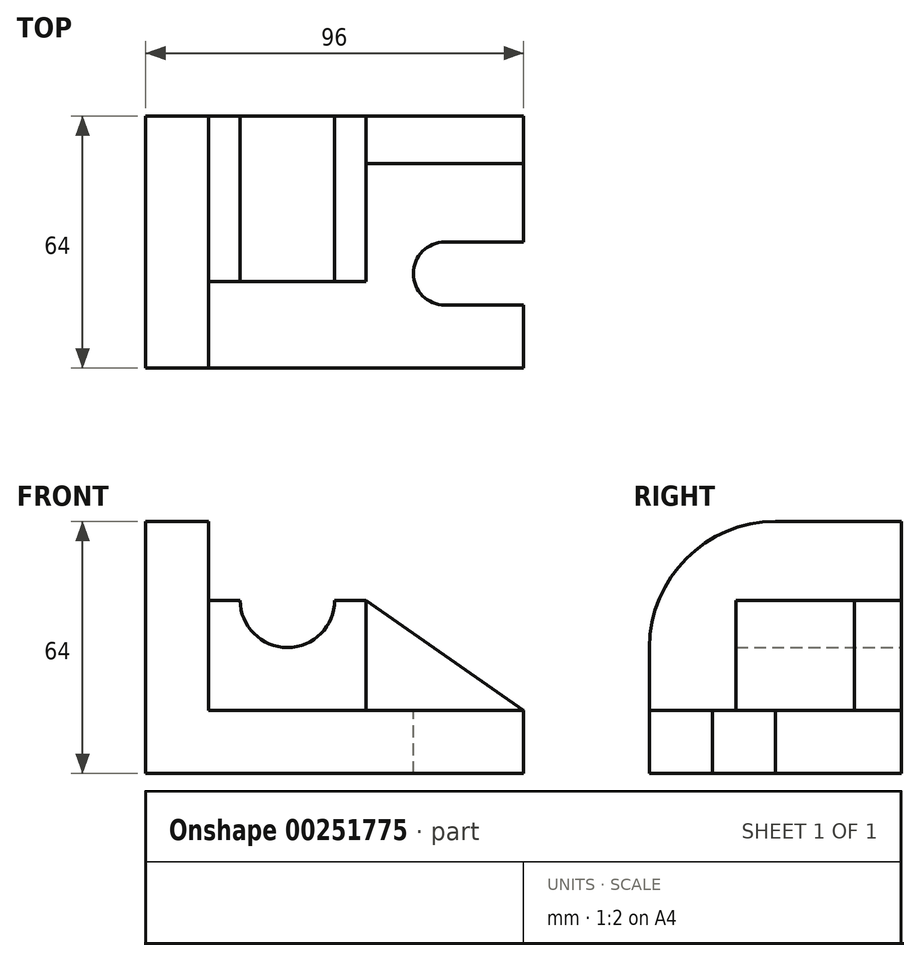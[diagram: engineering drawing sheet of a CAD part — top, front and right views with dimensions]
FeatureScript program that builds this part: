
annotation { "Feature Type Name" : "Feature", "Feature Type Description" : "" }
export const myFeature = defineFeature(function(context is Context, id is Id, definition is map)
    precondition{}
    {
        {
            var Q0;
            Q0=qCreatedBy(makeId("Front.planeOp"),FACE);
            var sketch = newSketch(context, id + "F0", { "sketchPlane" : qUnion([Q0])});
            skLineSegment(sketch, "E0.bottom", {"start": v(48, -8) * mm, "end": v(-48, -8) * mm});
            skLineSegment(sketch, "E0.top", {"start": v(48, 8) * mm, "end": v(-48, 8) * mm});
            skLineSegment(sketch, "E0.left", {"start": v(48, -8) * mm, "end": v(48, 8) * mm});
            skLineSegment(sketch, "E0.right", {"start": v(-48, -8) * mm, "end": v(-48, 8) * mm});
            skPoint(sketch, "E0.middle", {"position": v(0, 0) * mm});
            skLineSegment(sketch, "E1.bottom", {"start": v(-48, 8) * mm, "end": v(-32, 8) * mm});
            skLineSegment(sketch, "E1.top", {"start": v(-48, 56) * mm, "end": v(-32, 56) * mm});
            skLineSegment(sketch, "E1.left", {"start": v(-48, 8) * mm, "end": v(-48, 56) * mm});
            skLineSegment(sketch, "E1.right", {"start": v(-32, 8) * mm, "end": v(-32, 56) * mm});
            skSolve(sketch);
        }
        {
            var Q0;
            Q0 = qSketchRegion(id + "F0", true);
            extrude(context, id + "F1", {"entities" : qUnion([Q0]), "endBound" : BoundingType.SYMMETRIC, "oppositeDirection" : true, "depth" : 64 * mm});
        }
        {
            var Q0;
            Q0=makeQuery(id+"F1.opExtrude","CAP_EDGE",EDGE,{"disambiguationData":[OSD([sQuery(id+"F0.wireOp",EDGE,"E1.top")])],"isStart":true});
            fillet(context, id + "F2", {"entities" : qUnion([Q0]), "radius" : 32 * mm, "tangentPropagation" : true, "allowEdgeOverflow" : false});
        }
        {
            var Q0;
            Q0=makeQuery(id+"F1.opExtrude","CAP_FACE",FACE,{"disambiguationData":[OSD([sQuery(id+"F0.wireOp",EDGE,"E0.bottom"),sQuery(id+"F0.wireOp",EDGE,"E0.top"),sQuery(id+"F0.wireOp",EDGE,"E0.left"),sQuery(id+"F0.wireOp",EDGE,"E0.right"),sQuery(id+"F0.wireOp",EDGE,"E1.top"),sQuery(id+"F0.wireOp",EDGE,"E1.left"),sQuery(id+"F0.wireOp",EDGE,"E1.right")])],"isStart":false});
            var sketch = newSketch(context, id + "F3", { "sketchPlane" : qUnion([Q0])});
            skLineSegment(sketch, "E2", {"start": v(32, 36) * mm, "end": v(-8, 36) * mm});
            skLineSegment(sketch, "E3", {"start": v(-8, 36) * mm, "end": v(-8, 8) * mm});
            skLineSegment(sketch, "E4.0", {"start": v(32, 8) * mm, "end": v(32, 36) * mm});
            skLineSegment(sketch, "E5.0", {"start": v(-8, 8) * mm, "end": v(32, 8) * mm});
            skPoint(sketch, "E6.orphan", {"position": v(32, 56) * mm});
            skPoint(sketch, "E7.orphan", {"position": v(-48, 8) * mm});
            skSolve(sketch);
        }
        {
            var Q0;
            Q0 = qSketchRegion(id + "F3", true);
            extrude(context, id + "F4", {"entities" : qUnion([Q0]), "operationType" : NewBodyOperationType.ADD, "oppositeDirection" : true, "depth" : 42 * mm});
        }
        {
            var Q0;
            Q0=makeQuery(id+"F4.boolean.opBoolean","MERGE",FACE,{"derivedFrom":[makeQuery(id+"F1.opExtrude","CAP_FACE",FACE,{"disambiguationData":[OSD([sQuery(id+"F0.wireOp",EDGE,"E0.bottom"),sQuery(id+"F0.wireOp",EDGE,"E0.top"),sQuery(id+"F0.wireOp",EDGE,"E0.left"),sQuery(id+"F0.wireOp",EDGE,"E0.right"),sQuery(id+"F0.wireOp",EDGE,"E1.top"),sQuery(id+"F0.wireOp",EDGE,"E1.left"),sQuery(id+"F0.wireOp",EDGE,"E1.right")])],"isStart":false}),makeQuery(id+"F4.opExtrude","CAP_FACE",FACE,{"disambiguationData":[OSD([sQuery(id+"F3.wireOp",EDGE,"E2"),sQuery(id+"F3.wireOp",EDGE,"E3"),sQuery(id+"F3.wireOp",EDGE,"E4.0"),sQuery(id+"F3.wireOp",EDGE,"E5.0")])],"isStart":true})]});
            var sketch = newSketch(context, id + "F5", { "sketchPlane" : qUnion([Q0])});
            skArc(sketch, "E8", {"start": v(0, 36) * mm, "mid": v(12, 24) * mm, "end": v(24, 36) * mm});
            skLineSegment(sketch, "E9.0", {"start": v(24, 36) * mm, "end": v(0, 36) * mm});
            skPoint(sketch, "E10.orphan", {"position": v(32, 36) * mm});
            skPoint(sketch, "E11.orphan", {"position": v(-8, 36) * mm});
            skSolve(sketch);
        }
        {
            var Q0;
            Q0 = qSketchRegion(id + "F5", true);
            extrude(context, id + "F6", {"entities" : qUnion([Q0]), "operationType" : NewBodyOperationType.REMOVE, "endBound" : BoundingType.THROUGH_ALL, "oppositeDirection" : true, "depth" : 25 * mm});
        }
        {
            var Q0;
            Q0=makeQuery(id+"F4.boolean.opBoolean","MERGE",FACE,{"derivedFrom":[makeQuery(id+"F1.opExtrude","CAP_FACE",FACE,{"disambiguationData":[OSD([sQuery(id+"F0.wireOp",EDGE,"E0.bottom"),sQuery(id+"F0.wireOp",EDGE,"E0.top"),sQuery(id+"F0.wireOp",EDGE,"E0.left"),sQuery(id+"F0.wireOp",EDGE,"E0.right"),sQuery(id+"F0.wireOp",EDGE,"E1.top"),sQuery(id+"F0.wireOp",EDGE,"E1.left"),sQuery(id+"F0.wireOp",EDGE,"E1.right")])],"isStart":false}),makeQuery(id+"F4.opExtrude","CAP_FACE",FACE,{"disambiguationData":[OSD([sQuery(id+"F3.wireOp",EDGE,"E2"),sQuery(id+"F3.wireOp",EDGE,"E3"),sQuery(id+"F3.wireOp",EDGE,"E4.0"),sQuery(id+"F3.wireOp",EDGE,"E5.0")])],"isStart":true})]});
            var sketch = newSketch(context, id + "F7", { "sketchPlane" : qUnion([Q0])});
            skLineSegment(sketch, "E12", {"start": v(-8, 36) * mm, "end": v(-48, 8) * mm});
            skLineSegment(sketch, "E13.0.2", {"start": v(-8, 36) * mm, "end": v(-8, 8) * mm});
            skLineSegment(sketch, "E13.0.3", {"start": v(-8, 8) * mm, "end": v(-48, 8) * mm});
            skPoint(sketch, "E13.0.0.end.orphan", {"position": v(0, 36) * mm});
            skPoint(sketch, "E13.0.9.end.orphan", {"position": v(24, 36) * mm});
            skPoint(sketch, "E13.0.8.end.orphan", {"position": v(32, 36) * mm});
            skPoint(sketch, "E13.0.7.end.orphan", {"position": v(32, 56) * mm});
            skPoint(sketch, "E13.0.6.end.orphan", {"position": v(48, 56) * mm});
            skPoint(sketch, "E13.0.5.end.orphan", {"position": v(48, -8) * mm});
            skPoint(sketch, "E13.0.4.end.orphan", {"position": v(-48, -8) * mm});
            skSolve(sketch);
        }
        {
            var Q0;
            Q0 = qSketchRegion(id + "F7", true);
            extrude(context, id + "F8", {"entities" : qUnion([Q0]), "oppositeDirection" : true, "depth" : 12 * mm});
        }
        {
            var Q0;
            Q0=makeQuery(id+"F1.opExtrude","SWEPT_FACE",FACE,{"disambiguationData":[OSD([sQuery(id+"F0.wireOp",EDGE,"E0.top")])]});
            var sketch = newSketch(context, id + "F9", { "sketchPlane" : qUnion([Q0])});
            skLineSegment(sketch, "E14.bottom", {"start": v(48, 0) * mm, "end": v(28, 0) * mm});
            skLineSegment(sketch, "E14.top", {"start": v(48, -16) * mm, "end": v(28, -16) * mm});
            skLineSegment(sketch, "E14.left", {"start": v(48, 0) * mm, "end": v(48, -16) * mm});
            skCircle(sketch, "E15", {"center": v(28, -8) * mm, "radius": 8 * mm});
            skSolve(sketch);
        }
        {
            var Q0;
            Q0 = qSketchRegion(id + "F9", true);
            extrude(context, id + "F10", {"entities" : qUnion([Q0]), "operationType" : NewBodyOperationType.REMOVE, "oppositeDirection" : true, "depth" : 25 * mm});
        }
    });
